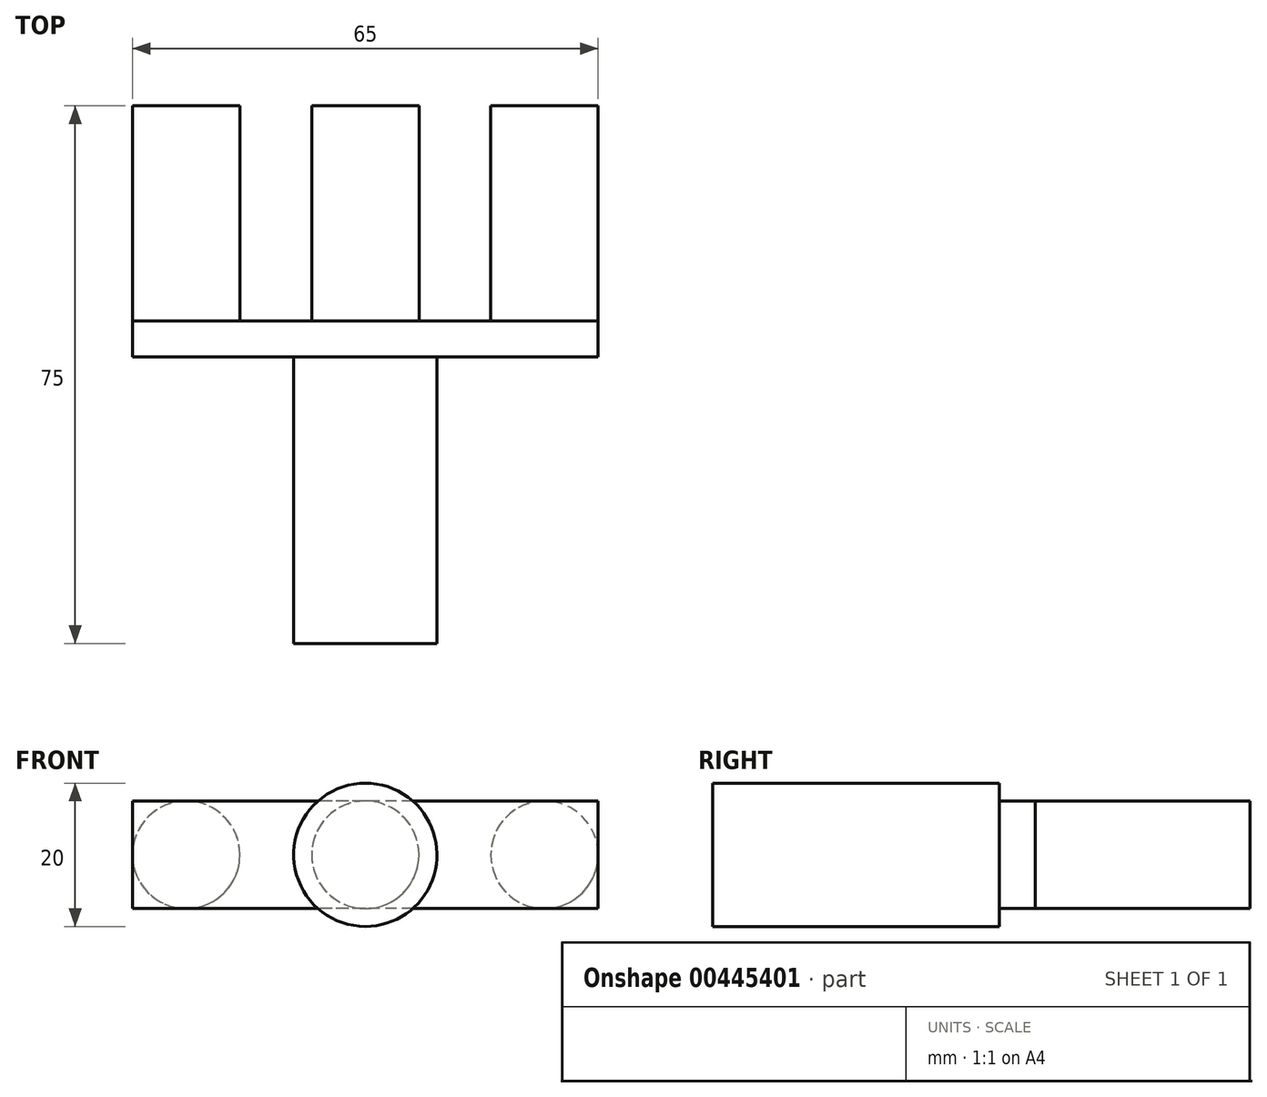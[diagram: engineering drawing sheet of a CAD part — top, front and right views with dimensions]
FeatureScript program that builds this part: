
annotation { "Feature Type Name" : "Feature", "Feature Type Description" : "" }
export const myFeature = defineFeature(function(context is Context, id is Id, definition is map)
    precondition{}
    {
        {
            var Q0;
            Q0=qCreatedBy(makeId("Front.planeOp"),FACE);
            var sketch = newSketch(context, id + "F0", { "sketchPlane" : qUnion([Q0])});
            skLineSegment(sketch, "E0.bottom", {"start": v(32.5, 7.5) * mm, "end": v(-32.5, 7.5) * mm});
            skLineSegment(sketch, "E0.top", {"start": v(32.5, -7.5) * mm, "end": v(-32.5, -7.5) * mm});
            skLineSegment(sketch, "E0.left", {"start": v(32.5, 7.5) * mm, "end": v(32.5, -7.5) * mm});
            skLineSegment(sketch, "E0.right", {"start": v(-32.5, 7.5) * mm, "end": v(-32.5, -7.5) * mm});
            skPoint(sketch, "E0.middle", {"position": v(0, 0) * mm});
            skSolve(sketch);
        }
        {
            var Q0;
            Q0 = qSketchRegion(id + "F0", true);
            extrude(context, id + "F1", {"entities" : qUnion([Q0]), "depth" : 5 * mm});
        }
        {
            var Q0;
            Q0=makeQuery(id+"F1.opExtrude","CAP_FACE",FACE,{"disambiguationData":[OSD([sQuery(id+"F0.wireOp",EDGE,"E0.bottom"),sQuery(id+"F0.wireOp",EDGE,"E0.top"),sQuery(id+"F0.wireOp",EDGE,"E0.left"),sQuery(id+"F0.wireOp",EDGE,"E0.right")])],"isStart":true});
            var sketch = newSketch(context, id + "F2", { "sketchPlane" : qUnion([Q0])});
            skCircle(sketch, "E1", {"center": v(0, 0) * mm, "radius": 7.5 * mm});
            skLineSegment(sketch, "E2", {"start": v(7.5, 0) * mm, "end": v(25, 0) * mm});
            skLineSegment(sketch, "E3", {"start": v(-7.5, 0) * mm, "end": v(-25, 0) * mm});
            skCircle(sketch, "E4", {"center": v(-25, 0) * mm, "radius": 7.5 * mm});
            skCircle(sketch, "E5", {"center": v(25, 0) * mm, "radius": 7.5 * mm});
            skSolve(sketch);
        }
        {
            var Q0;
            Q0 = qSketchRegion(id + "F2", true);
            extrude(context, id + "F3", {"entities" : qUnion([Q0]), "operationType" : NewBodyOperationType.ADD, "depth" : 30 * mm});
        }
        {
            var Q0;
            Q0=makeQuery(id+"F1.opExtrude","CAP_FACE",FACE,{"disambiguationData":[OSD([sQuery(id+"F0.wireOp",EDGE,"E0.bottom"),sQuery(id+"F0.wireOp",EDGE,"E0.top"),sQuery(id+"F0.wireOp",EDGE,"E0.left"),sQuery(id+"F0.wireOp",EDGE,"E0.right")])],"isStart":false});
            var sketch = newSketch(context, id + "F4", { "sketchPlane" : qUnion([Q0])});
            skCircle(sketch, "E6", {"center": v(0, 0) * mm, "radius": 10 * mm});
            skSolve(sketch);
        }
        {
            var Q0;
            Q0 = qSketchRegion(id + "F4", true);
            extrude(context, id + "F5", {"entities" : qUnion([Q0]), "operationType" : NewBodyOperationType.ADD, "depth" : 40 * mm});
        }
    });
